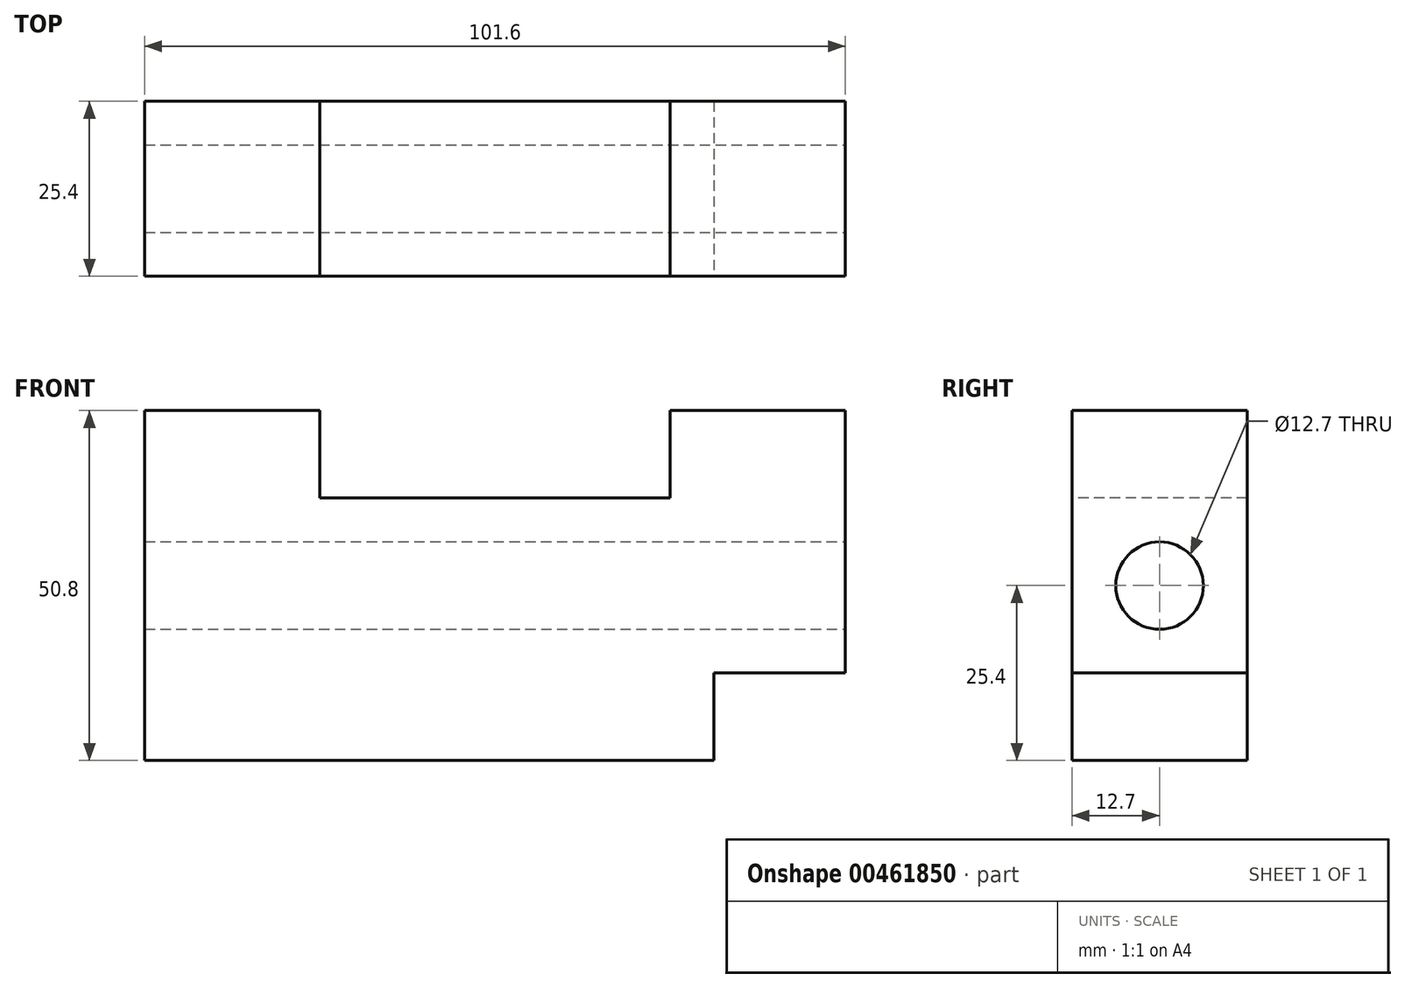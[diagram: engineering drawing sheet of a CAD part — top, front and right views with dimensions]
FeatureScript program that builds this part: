
annotation { "Feature Type Name" : "Feature", "Feature Type Description" : "" }
export const myFeature = defineFeature(function(context is Context, id is Id, definition is map)
    precondition{}
    {
        {
            var Q0;
            Q0=qCreatedBy(makeId("Front.planeOp"),FACE);
            var sketch = newSketch(context, id + "F0", { "sketchPlane" : qUnion([Q0])});
            skLineSegment(sketch, "E0.bottom", {"start": v(-50.8, 25.4) * mm, "end": v(50.8, 25.4) * mm});
            skLineSegment(sketch, "E0.top", {"start": v(-50.8, -25.4) * mm, "end": v(50.8, -25.4) * mm});
            skLineSegment(sketch, "E0.left", {"start": v(-50.8, 25.4) * mm, "end": v(-50.8, -25.4) * mm});
            skLineSegment(sketch, "E0.right", {"start": v(50.8, 25.4) * mm, "end": v(50.8, -25.4) * mm});
            skPoint(sketch, "E0.middle", {"position": v(0, 0) * mm});
            skSolve(sketch);
        }
        {
            var Q0;
            Q0=makeQuery(id+"F0.imprint","IMPRINT",FACE,{"disambiguationData":[TD([[makeQuery(id+"F0.imprint","IMPRINT",EDGE,{"derivedFrom":sQuery(id+"F0.wireOp",EDGE,"E0.bottom")}),-1.0]])]});
            extrude(context, id + "F1", {"entities" : qUnion([Q0]), "depth" : 25.4 * mm});
        }
        {
            var Q0;
            Q0=makeQuery(id+"F1.opExtrude","CAP_FACE",FACE,{"disambiguationData":[OSD([sQuery(id+"F0.wireOp",EDGE,"E0.bottom"),sQuery(id+"F0.wireOp",EDGE,"E0.top"),sQuery(id+"F0.wireOp",EDGE,"E0.left"),sQuery(id+"F0.wireOp",EDGE,"E0.right")])],"isStart":false});
            var sketch = newSketch(context, id + "F2", { "sketchPlane" : qUnion([Q0])});
            skLineSegment(sketch, "E1.bottom", {"start": v(-25.4, 25.4) * mm, "end": v(25.4, 25.4) * mm});
            skLineSegment(sketch, "E1.top", {"start": v(-25.4, 12.7) * mm, "end": v(25.4, 12.7) * mm});
            skLineSegment(sketch, "E1.left", {"start": v(-25.4, 25.4) * mm, "end": v(-25.4, 12.7) * mm});
            skLineSegment(sketch, "E1.right", {"start": v(25.4, 25.4) * mm, "end": v(25.4, 12.7) * mm});
            skSolve(sketch);
        }
        {
            var Q0;
            Q0 = qSketchRegion(id + "F2", true);
            extrude(context, id + "F3", {"entities" : qUnion([Q0]), "operationType" : NewBodyOperationType.REMOVE, "endBound" : BoundingType.THROUGH_ALL, "oppositeDirection" : true, "depth" : 25.4 * mm});
        }
        {
            var Q0;
            Q0=makeQuery(id+"F1.opExtrude","CAP_FACE",FACE,{"disambiguationData":[OSD([sQuery(id+"F0.wireOp",EDGE,"E0.bottom"),sQuery(id+"F0.wireOp",EDGE,"E0.top"),sQuery(id+"F0.wireOp",EDGE,"E0.left"),sQuery(id+"F0.wireOp",EDGE,"E0.right")])],"isStart":false});
            var sketch = newSketch(context, id + "F4", { "sketchPlane" : qUnion([Q0])});
            skLineSegment(sketch, "E2.bottom", {"start": v(50.8, -25.4) * mm, "end": v(31.75, -25.4) * mm});
            skLineSegment(sketch, "E2.top", {"start": v(50.8, -12.7) * mm, "end": v(31.75, -12.7) * mm});
            skLineSegment(sketch, "E2.left", {"start": v(50.8, -25.4) * mm, "end": v(50.8, -12.7) * mm});
            skLineSegment(sketch, "E2.right", {"start": v(31.75, -25.4) * mm, "end": v(31.75, -12.7) * mm});
            skSolve(sketch);
        }
        {
            var Q0;
            Q0 = qSketchRegion(id + "F4", true);
            extrude(context, id + "F5", {"entities" : qUnion([Q0]), "operationType" : NewBodyOperationType.REMOVE, "endBound" : BoundingType.THROUGH_ALL, "oppositeDirection" : true, "depth" : 25.4 * mm});
        }
        {
            var Q0;
            Q0=makeQuery(id+"F1.opExtrude","SWEPT_FACE",FACE,{"disambiguationData":[OSD([sQuery(id+"F0.wireOp",EDGE,"E0.right")])]});
            var sketch = newSketch(context, id + "F6", { "sketchPlane" : qUnion([Q0])});
            skCircle(sketch, "E3", {"center": v(-12.7, 0) * mm, "radius": 6.35 * mm});
            skPoint(sketch, "E3.centerSnap0", {"position": v(-12.7, 25.4) * mm});
            skSolve(sketch);
        }
        {
            var Q0;
            Q0 = qSketchRegion(id + "F6", true);
            extrude(context, id + "F7", {"entities" : qUnion([Q0]), "operationType" : NewBodyOperationType.REMOVE, "endBound" : BoundingType.THROUGH_ALL, "oppositeDirection" : true, "depth" : 25.4 * mm});
        }
    });
